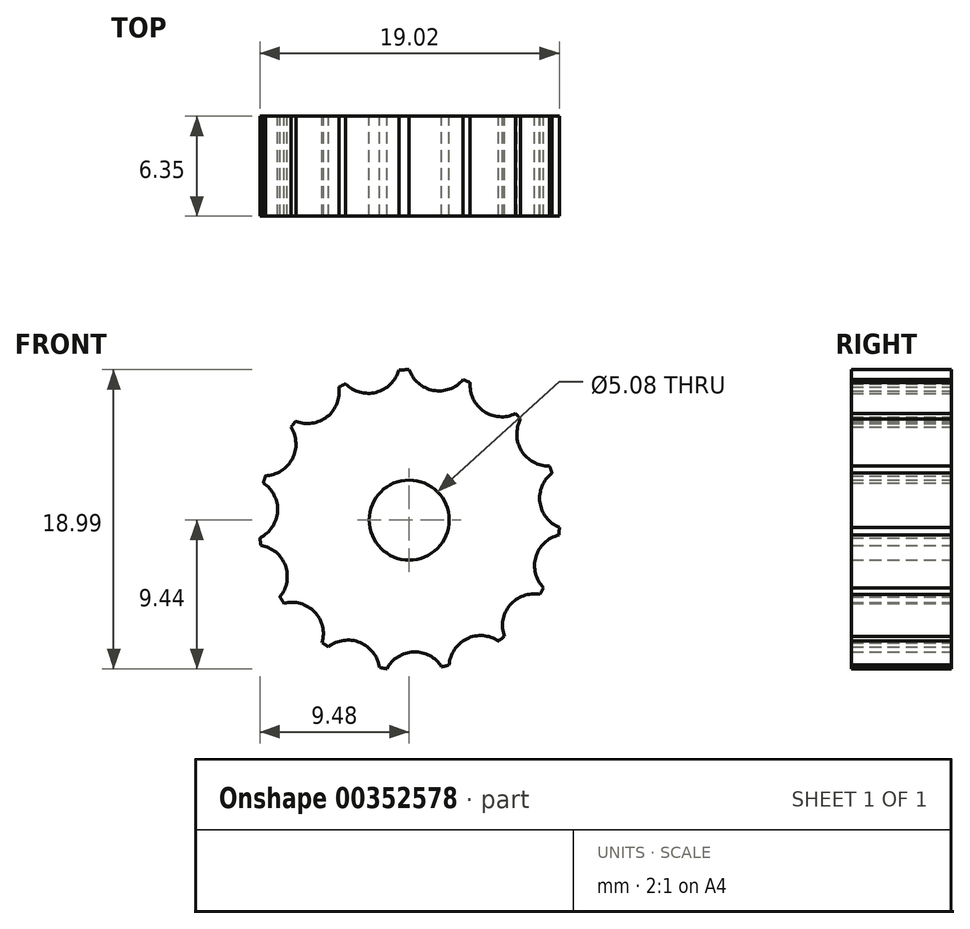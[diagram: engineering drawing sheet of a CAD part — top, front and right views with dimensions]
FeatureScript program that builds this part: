
annotation { "Feature Type Name" : "Feature", "Feature Type Description" : "" }
export const myFeature = defineFeature(function(context is Context, id is Id, definition is map)
    precondition{}
    {
        {
            var Q0;
            Q0=qCreatedBy(makeId("Front.planeOp"),FACE);
            var sketch = newSketch(context, id + "F0", { "sketchPlane" : qUnion([Q0])});
            skCircle(sketch, "E0", {"center": v(0, 0) * mm, "radius": 2.54 * mm});
            skArc(sketch, "E1", {"start": v(-7.2, 6.27) * mm, "mid": v(-7.36, 6.1) * mm, "end": v(-7.5, 5.9) * mm});
            skArc(sketch, "E2", {"start": v(0, 9.55) * mm, "mid": v(1.53, 8.24) * mm, "end": v(3.43, 8.91) * mm});
            skArc(sketch, "E3.1.0", {"start": v(3.87, 8.73) * mm, "mid": v(4.74, 6.91) * mm, "end": v(6.75, 6.76) * mm});
            skArc(sketch, "E3.2.0", {"start": v(7.08, 6.4) * mm, "mid": v(7.14, 4.4) * mm, "end": v(8.9, 3.44) * mm});
            skArc(sketch, "E3.3.0", {"start": v(9.07, 2.99) * mm, "mid": v(8.3, 1.12) * mm, "end": v(9.54, -0.47) * mm});
            skArc(sketch, "E3.4.0", {"start": v(9.5, -0.95) * mm, "mid": v(8.05, -2.34) * mm, "end": v(8.53, -4.3) * mm});
            skArc(sketch, "E3.5.0", {"start": v(8.3, -4.72) * mm, "mid": v(6.4, -5.4) * mm, "end": v(6.05, -7.39) * mm});
            skArc(sketch, "E3.6.0", {"start": v(5.67, -7.68) * mm, "mid": v(3.66, -7.54) * mm, "end": v(2.54, -9.2) * mm});
            skArc(sketch, "E3.7.0", {"start": v(2.07, -9.32) * mm, "mid": v(0.3, -8.38) * mm, "end": v(-1.42, -9.44) * mm});
            skArc(sketch, "E3.8.0", {"start": v(-1.9, -9.36) * mm, "mid": v(-3.13, -7.77) * mm, "end": v(-5.13, -8.06) * mm});
            skArc(sketch, "E3.9.0", {"start": v(-5.53, -7.79) * mm, "mid": v(-6.02, -5.83) * mm, "end": v(-7.95, -5.29) * mm});
            skArc(sketch, "E3.10.0", {"start": v(-8.21, -4.88) * mm, "mid": v(-7.86, -2.9) * mm, "end": v(-9.41, -1.6) * mm});
            skArc(sketch, "E3.11.0", {"start": v(-9.48, -1.13) * mm, "mid": v(-8.36, 0.55) * mm, "end": v(-9.26, 2.35) * mm});
            skArc(sketch, "E3.12.0", {"start": v(-9.13, 2.82) * mm, "mid": v(-7.42, 3.89) * mm, "end": v(-7.5, 5.9) * mm});
            skArc(sketch, "E3.13.0", {"start": v(-7.2, 6.27) * mm, "mid": v(-5.2, 6.57) * mm, "end": v(-4.47, 8.44) * mm});
            skArc(sketch, "E3.14.0", {"start": v(-4.04, 8.66) * mm, "mid": v(-2.1, 8.11) * mm, "end": v(-0.66, 9.53) * mm});
            skLineSegment(sketch, "E3.anchor1", {"start": v(0, 0) * mm, "end": v(0, 9.55) * mm, "construction": true});
            skLineSegment(sketch, "E3.anchor2", {"start": v(0, 0) * mm, "end": v(-4.04, 8.66) * mm, "construction": true});
            skArc(sketch, "E4.trimOffspring", {"start": v(-4.04, 8.66) * mm, "mid": v(-4.25, 8.55) * mm, "end": v(-4.47, 8.44) * mm});
            skArc(sketch, "E5.trimOffspring", {"start": v(0, 9.55) * mm, "mid": v(-0.33, 9.54) * mm, "end": v(-0.66, 9.53) * mm});
            skArc(sketch, "E6.trimOffspring", {"start": v(-9.13, 2.82) * mm, "mid": v(-9.2, 2.58) * mm, "end": v(-9.26, 2.35) * mm});
            skArc(sketch, "E7.trimOffspring", {"start": v(3.87, 8.73) * mm, "mid": v(3.65, 8.82) * mm, "end": v(3.43, 8.91) * mm});
            skArc(sketch, "E8.trimOffspring", {"start": v(7.08, 6.4) * mm, "mid": v(6.92, 6.59) * mm, "end": v(6.75, 6.76) * mm});
            skArc(sketch, "E9.trimOffspring", {"start": v(-9.48, -1.13) * mm, "mid": v(-9.45, -1.37) * mm, "end": v(-9.41, -1.6) * mm});
            skArc(sketch, "E10.trimOffspring", {"start": v(-8.21, -4.88) * mm, "mid": v(-8.08, -5.08) * mm, "end": v(-7.95, -5.29) * mm});
            skArc(sketch, "E11.trimOffspring", {"start": v(-5.53, -7.79) * mm, "mid": v(-5.33, -7.93) * mm, "end": v(-5.13, -8.06) * mm});
            skArc(sketch, "E12.trimOffspring", {"start": v(-1.9, -9.36) * mm, "mid": v(-1.65, -9.4) * mm, "end": v(-1.42, -9.44) * mm});
            skArc(sketch, "E13.trimOffspring", {"start": v(2.07, -9.32) * mm, "mid": v(2.3, -9.27) * mm, "end": v(2.54, -9.2) * mm});
            skArc(sketch, "E14.trimOffspring", {"start": v(5.67, -7.68) * mm, "mid": v(5.86, -7.54) * mm, "end": v(6.05, -7.39) * mm});
            skArc(sketch, "E15.trimOffspring", {"start": v(9.5, -0.95) * mm, "mid": v(9.52, -0.71) * mm, "end": v(9.54, -0.47) * mm});
            skArc(sketch, "E16.trimOffspring", {"start": v(9.07, 2.99) * mm, "mid": v(9, 3.21) * mm, "end": v(8.9, 3.44) * mm});
            skArc(sketch, "E17", {"start": v(8.3, -4.72) * mm, "mid": v(8.42, -4.51) * mm, "end": v(8.53, -4.3) * mm});
            skSolve(sketch);
        }
        {
            var Q0;
            Q0=makeQuery(id+"F0.imprint","IMPRINT",FACE,{"disambiguationData":[TD([[makeQuery(id+"F0.imprint","IMPRINT",EDGE,{"derivedFrom":sQuery(id+"F0.wireOp",EDGE,"E0")}),-1.0]])]});
            extrude(context, id + "F1", {"entities" : qUnion([Q0]), "depth" : 6.35 * mm});
        }
    });
